# Revit family: RapidBeam_StandardLap_LargeSpan
name_source: partatom
category: Generic Models
units: mm (PartAtom-declared; Revit-internal decimal feet)

## family parameters
Always vertical = Yes
Can host rebar = No
Cut with Voids When Loaded = No
OmniClass Number = 23.25.30.11.14.14
OmniClass Title = Beams
Part Type = Normal
Room Calculation Point = No
Round Connector Dimension = Use Diameter
Shared = No
Work Plane-Based = No

## types (1)
- RapidBeam_StandardLap_LargeSpan
    Default Elevation = 2000 mm  [stored 6.56168 ft]
    Description = Rapid Beam Bridging Beam for non-structural restraints.
    End Bracket Material = Steel Galvanised
    IFCExportAs = IfcBeam
    IFCExportType = BEAM
    IFCName = Rapid Beam Standard lap Large span
    Length = 1600 mm
    Manufacturer = Cold Rolled Systems
    Masterspec CBI = 3421
    Material = Hot dipped galvanised mild steel, Manufactured in New Zealand.
    Model = Rapid Beam Standard lap Large span.
    Rapid Beam Material = Steel Galvanised
    Span = 1600 mm
    Span Max Min = 1800mm max span, 1500mm min span.
    URL = https://www.tris.co.nz

note: [stored X ft] marks values corroborated as IEEE doubles in the binary element streams (Revit-internal decimal feet)

## geometry (parser evidence)
native form markers: Sweep x7
no freeform markers — native parametric forms only
